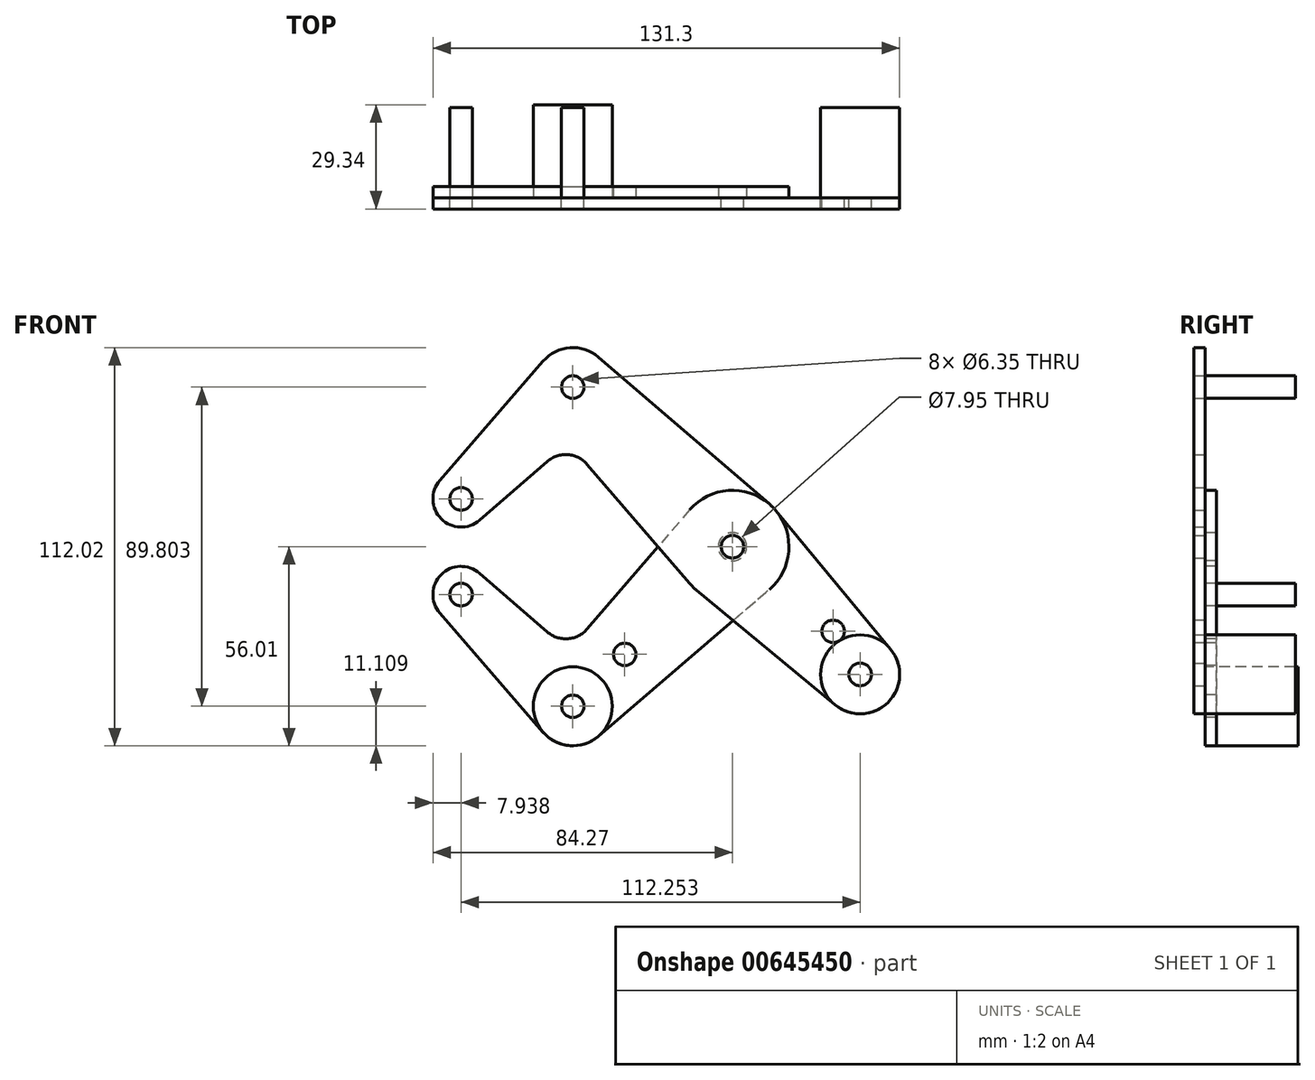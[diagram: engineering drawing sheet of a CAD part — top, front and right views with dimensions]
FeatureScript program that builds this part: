
annotation { "Feature Type Name" : "Feature", "Feature Type Description" : "" }
export const myFeature = defineFeature(function(context is Context, id is Id, definition is map)
    precondition{}
    {
        {
            var Q0;
            Q0=qCreatedBy(makeId("Front.planeOp"),FACE);
            var sketch = newSketch(context, id + "F0", { "sketchPlane" : qUnion([Q0])});
            skCircle(sketch, "E0", {"center": v(-76.33, 13.47) * mm, "radius": 7.94 * mm});
            skCircle(sketch, "E1", {"center": v(-44.9, 44.9) * mm, "radius": 11.11 * mm});
            skCircle(sketch, "E2", {"center": v(0, 0) * mm, "radius": 15.88 * mm});
            skCircle(sketch, "E3", {"center": v(35.92, -35.92) * mm, "radius": 11.11 * mm});
            skCircle(sketch, "E4", {"center": v(35.92, -35.92) * mm, "radius": 3.18 * mm});
            skCircle(sketch, "E5", {"center": v(0, 0) * mm, "radius": 3.18 * mm});
            skCircle(sketch, "E6", {"center": v(-44.9, 44.9) * mm, "radius": 3.18 * mm});
            skCircle(sketch, "E7", {"center": v(-76.33, 13.47) * mm, "radius": 3.18 * mm});
            skLineSegment(sketch, "E8", {"start": v(-76.33, 13.47) * mm, "end": v(-44.9, 44.9) * mm, "construction": true});
            skLineSegment(sketch, "E9", {"start": v(-44.9, 44.9) * mm, "end": v(0, 0) * mm, "construction": true});
            skLineSegment(sketch, "E10", {"start": v(0, 0) * mm, "end": v(35.92, -35.92) * mm, "construction": true});
            skCircle(sketch, "E11", {"center": v(28.32, -23.83) * mm, "radius": 3.18 * mm});
            skCircle(sketch, "E12", {"center": v(0, 0) * mm, "radius": 3.98 * mm});
            skLineSegment(sketch, "E13", {"start": v(-82.33, 18.67) * mm, "end": v(-53.3, 52.18) * mm});
            skLineSegment(sketch, "E14", {"start": v(-71.13, 7.47) * mm, "end": v(-52.08, 23.98) * mm});
            skLineSegment(sketch, "E15", {"start": v(-37.66, 53.33) * mm, "end": v(10.35, 12.04) * mm});
            skLineSegment(sketch, "E16", {"start": v(-53.33, 37.66) * mm, "end": v(-52.78, 37.02) * mm});
            skLineSegment(sketch, "E17", {"start": v(12.23, 10.12) * mm, "end": v(44.48, -28.83) * mm});
            skLineSegment(sketch, "E18", {"start": v(-10.12, -12.23) * mm, "end": v(28.83, -44.48) * mm});
            skLineSegment(sketch, "E19.trimOffspring", {"start": v(-40.85, 23.15) * mm, "end": v(-12.04, -10.35) * mm});
            skLineSegment(sketch, "E20", {"start": v(0, 0) * mm, "end": v(-44.9, -44.9) * mm, "construction": true});
            skLineSegment(sketch, "E21", {"start": v(-44.9, -44.9) * mm, "end": v(-76.33, -13.47) * mm, "construction": true});
            skCircle(sketch, "E22", {"center": v(-44.9, -44.9) * mm, "radius": 11.11 * mm});
            skCircle(sketch, "E23", {"center": v(-44.9, -44.9) * mm, "radius": 3.18 * mm});
            skCircle(sketch, "E24", {"center": v(-76.33, -13.47) * mm, "radius": 7.94 * mm});
            skCircle(sketch, "E25", {"center": v(-76.33, -13.47) * mm, "radius": 3.18 * mm});
            skCircle(sketch, "E26", {"center": v(-30.3, -30.3) * mm, "radius": 3.18 * mm});
            skLineSegment(sketch, "E27", {"start": v(-12.04, 10.35) * mm, "end": v(-40.85, -23.15) * mm});
            skLineSegment(sketch, "E28", {"start": v(-82.33, -18.67) * mm, "end": v(-53.3, -52.18) * mm});
            skLineSegment(sketch, "E29", {"start": v(-37.66, -53.33) * mm, "end": v(10.35, -12.04) * mm});
            skLineSegment(sketch, "E30.trimOffspring", {"start": v(-52.78, -37.02) * mm, "end": v(-53.33, -37.66) * mm});
            skLineSegment(sketch, "E31.trimOffspring", {"start": v(-52.08, -23.98) * mm, "end": v(-71.13, -7.47) * mm});
            skArc(sketch, "E32.filletArc", {"start": v(-52.08, -23.98) * mm, "mid": v(-46.3, -25.9) * mm, "end": v(-40.85, -23.15) * mm});
            skArc(sketch, "E33.filletArc", {"start": v(-40.85, 23.15) * mm, "mid": v(-46.3, 25.9) * mm, "end": v(-52.08, 23.98) * mm});
            skSolve(sketch);
        }
        {
            var Q0;
            {var subQ7=sQuery(id+"F0.wireOp",EDGE,"E13");Q0=makeQuery(id+"F0.imprint","IMPRINT",FACE,{"disambiguationData":[TD([[makeQuery(id+"F0.imprint","IMPRINT",EDGE,{"derivedFrom":subQ7}),-1.0]])]});}
            var Q1;
            Q1=makeQuery(id+"F0.imprint","IMPRINT",FACE,{"disambiguationData":[TD([[makeQuery(id+"F0.imprint","IMPRINT",EDGE,{"derivedFrom":sQuery(id+"F0.wireOp",EDGE,"E7")}),-1.0]])]});
            var Q2;
            Q2=makeQuery(id+"F0.imprint","IMPRINT",FACE,{"disambiguationData":[TD([[makeQuery(id+"F0.imprint","IMPRINT",EDGE,{"derivedFrom":sQuery(id+"F0.wireOp",EDGE,"E6")}),-1.0]])]});
            var Q3;
            Q3=makeQuery(id+"F0.imprint","IMPRINT",FACE,{"disambiguationData":[TD([[makeQuery(id+"F0.imprint","IMPRINT",EDGE,{"derivedFrom":sQuery(id+"F0.wireOp",EDGE,"E12")}),-1.0]])]});
            var Q4;
            {var subQ0=sQuery(id+"F0.wireOp",EDGE,"E19.trimOffspring");var subQ1=sQuery(id+"F0.wireOp",EDGE,"E2");var subQ2=makeQuery(id+"F0.imprint","INTERSECT",VERTEX,{"derivedFrom":[subQ1,subQ0]});Q4=makeQuery(id+"F0.imprint","IMPRINT",FACE,{"disambiguationData":[TD([[makeQuery(id+"F0.imprint","IMPRINT",EDGE,{"disambiguationData":[TD([[subQ2,1.0]])],"derivedFrom":subQ1}),-1.0]])]});}
            var Q5;
            {var subQ0=sQuery(id+"F0.wireOp",EDGE,"E11");Q5=makeQuery(id+"F0.imprint","IMPRINT",FACE,{"disambiguationData":[TD([[makeQuery(id+"F0.imprint","IMPRINT",EDGE,{"derivedFrom":subQ0}),-1.0]])]});}
            var Q6;
            Q6=makeQuery(id+"F0.imprint","IMPRINT",FACE,{"disambiguationData":[TD([[makeQuery(id+"F0.imprint","IMPRINT",EDGE,{"derivedFrom":sQuery(id+"F0.wireOp",EDGE,"E4")}),-1.0]])]});
            var Q7;
            {var subQ0=sQuery(id+"F0.wireOp",EDGE,"E18");var subQ1=sQuery(id+"F0.wireOp",EDGE,"E2");var subQ2=makeQuery(id+"F0.imprint","INTERSECT",VERTEX,{"derivedFrom":[subQ1,subQ0]});Q7=makeQuery(id+"F0.imprint","IMPRINT",FACE,{"disambiguationData":[TD([[makeQuery(id+"F0.imprint","IMPRINT",EDGE,{"disambiguationData":[TD([[subQ2,-1.0]])],"derivedFrom":subQ1}),-1.0]])]});}
            var Q8;
            Q8=makeQuery(id+"F0.imprint","IMPRINT",FACE,{"disambiguationData":[TD([[makeQuery(id+"F0.imprint","IMPRINT",EDGE,{"derivedFrom":sQuery(id+"F0.wireOp",EDGE,"E5")}),-1.0]])]});
            extrude(context, id + "F1", {"entities" : qUnion([Q0, Q1, Q2, Q3, Q4, Q5, Q6, Q7, Q8]), "depth" : 3.17 * mm, "offsetDistance" : 25.4 * mm});
        }
        {
            var Q0;
            Q0=makeQuery(id+"F0.imprint","IMPRINT",FACE,{"disambiguationData":[TD([[makeQuery(id+"F0.imprint","IMPRINT",EDGE,{"derivedFrom":sQuery(id+"F0.wireOp",EDGE,"E26")}),-1.0]])]});
            var Q1;
            Q1=makeQuery(id+"F0.imprint","IMPRINT",FACE,{"disambiguationData":[TD([[makeQuery(id+"F0.imprint","IMPRINT",EDGE,{"derivedFrom":sQuery(id+"F0.wireOp",EDGE,"E25")}),-1.0]])]});
            var Q2;
            Q2=makeQuery(id+"F0.imprint","IMPRINT",FACE,{"disambiguationData":[TD([[makeQuery(id+"F0.imprint","IMPRINT",EDGE,{"derivedFrom":sQuery(id+"F0.wireOp",EDGE,"E23")}),-1.0]])]});
            var Q3;
            Q3=makeQuery(id+"F0.imprint","IMPRINT",FACE,{"disambiguationData":[TD([[makeQuery(id+"F0.imprint","IMPRINT",EDGE,{"derivedFrom":sQuery(id+"F0.wireOp",EDGE,"E12")}),-1.0]])]});
            var Q4;
            {var subQ0=sQuery(id+"F0.wireOp",EDGE,"E19.trimOffspring");var subQ1=sQuery(id+"F0.wireOp",EDGE,"E2");var subQ2=makeQuery(id+"F0.imprint","INTERSECT",VERTEX,{"derivedFrom":[subQ1,subQ0]});Q4=makeQuery(id+"F0.imprint","IMPRINT",FACE,{"disambiguationData":[TD([[makeQuery(id+"F0.imprint","IMPRINT",EDGE,{"disambiguationData":[TD([[subQ2,1.0]])],"derivedFrom":subQ1}),-1.0]])]});}
            var Q5;
            {var subQ0=sQuery(id+"F0.wireOp",EDGE,"E18");var subQ1=sQuery(id+"F0.wireOp",EDGE,"E2");var subQ2=makeQuery(id+"F0.imprint","INTERSECT",VERTEX,{"derivedFrom":[subQ1,subQ0]});Q5=makeQuery(id+"F0.imprint","IMPRINT",FACE,{"disambiguationData":[TD([[makeQuery(id+"F0.imprint","IMPRINT",EDGE,{"disambiguationData":[TD([[subQ2,-1.0]])],"derivedFrom":subQ1}),-1.0]])]});}
            extrude(context, id + "F2", {"entities" : qUnion([Q0, Q1, Q2, Q3, Q4, Q5]), "oppositeDirection" : true, "depth" : 3.17 * mm, "offsetDistance" : 25.4 * mm});
        }
        {
            var Q0;
            Q0=qCreatedBy(makeId("Front.planeOp"),FACE);
            var sketch = newSketch(context, id + "F3", { "sketchPlane" : qUnion([Q0])});
            skCircle(sketch, "E34", {"center": v(-44.9, 44.9) * mm, "radius": 3.98 * mm});
            skCircle(sketch, "E35", {"center": v(35.92, -35.92) * mm, "radius": 11.11 * mm});
            skCircle(sketch, "E36", {"center": v(-44.9, -44.9) * mm, "radius": 11.11 * mm});
            skCircle(sketch, "E37", {"center": v(-76.33, -13.47) * mm, "radius": 3.98 * mm});
            skSolve(sketch);
        }
        {
            var Q0;
            Q0=makeQuery(id+"F0.imprint","IMPRINT",FACE,{"disambiguationData":[TD([[makeQuery(id+"F0.imprint","IMPRINT",EDGE,{"derivedFrom":sQuery(id+"F0.wireOp",EDGE,"E23")}),-1.0]])]});
            var Q1;
            Q1=makeQuery(id+"F0.imprint","IMPRINT",FACE,{"disambiguationData":[TD([[makeQuery(id+"F0.imprint","IMPRINT",EDGE,{"derivedFrom":sQuery(id+"F0.wireOp",EDGE,"E23")}),1.0]])]});
            extrude(context, id + "F4", {"entities" : qUnion([Q0, Q1]), "depth" : 0 * mm, "offsetDistance" : 25.4 * mm, "hasSecondDirection" : true, "secondDirectionOppositeDirection" : true, "secondDirectionDepth" : 26.16 * mm});
        }
        {
            var Q0;
            Q0=makeQuery(id+"F3.imprint","IMPRINT",FACE,{"disambiguationData":[TD([[makeQuery(id+"F3.imprint","IMPRINT",EDGE,{"derivedFrom":sQuery(id+"F3.wireOp",EDGE,"E35")}),1.0]])]});
            extrude(context, id + "F5", {"entities" : qUnion([Q0]), "depth" : 3.17 * mm, "offsetDistance" : 25.4 * mm, "hasSecondDirection" : true, "secondDirectionOppositeDirection" : true, "secondDirectionDepth" : 25.4 * mm});
        }
        {
            var Q0;
            Q0=makeQuery(id+"F0.imprint","IMPRINT",FACE,{"disambiguationData":[TD([[makeQuery(id+"F0.imprint","IMPRINT",EDGE,{"derivedFrom":sQuery(id+"F0.wireOp",EDGE,"E6")}),1.0]])]});
            extrude(context, id + "F6", {"entities" : qUnion([Q0]), "depth" : 3.17 * mm, "offsetDistance" : 25.4 * mm, "hasSecondDirection" : true, "secondDirectionOppositeDirection" : true, "secondDirectionDepth" : 25.4 * mm});
        }
        {
            var Q0;
            Q0=makeQuery(id+"F0.imprint","IMPRINT",FACE,{"disambiguationData":[TD([[makeQuery(id+"F0.imprint","IMPRINT",EDGE,{"derivedFrom":sQuery(id+"F0.wireOp",EDGE,"E25")}),1.0]])]});
            extrude(context, id + "F7", {"entities" : qUnion([Q0]), "depth" : 0 * mm, "offsetDistance" : 25.4 * mm, "hasSecondDirection" : true, "secondDirectionOppositeDirection" : true, "secondDirectionDepth" : 25.4 * mm});
        }
    });
